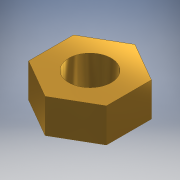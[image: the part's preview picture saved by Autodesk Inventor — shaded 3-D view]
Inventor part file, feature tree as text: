
AUTODESK INVENTOR PART (.ipt)
format: ipt  version: 2016 (Build 200138000, 138)  size: 107,520 bytes
history: native  units: mm
features: other x1, extrude x1, sketch x1
ambient origin geometry x8: Origin, YZ Plane, XZ Plane, XY Plane, X Axis, Y Axis, Z Axis, Center Point
bodies: Body1 (feature_tree)
feature tree (3):
  other  "ソリッド1"
  extrude  "押し出し1"  Depth=5.5mm
  sketch  "スケッチ1"
